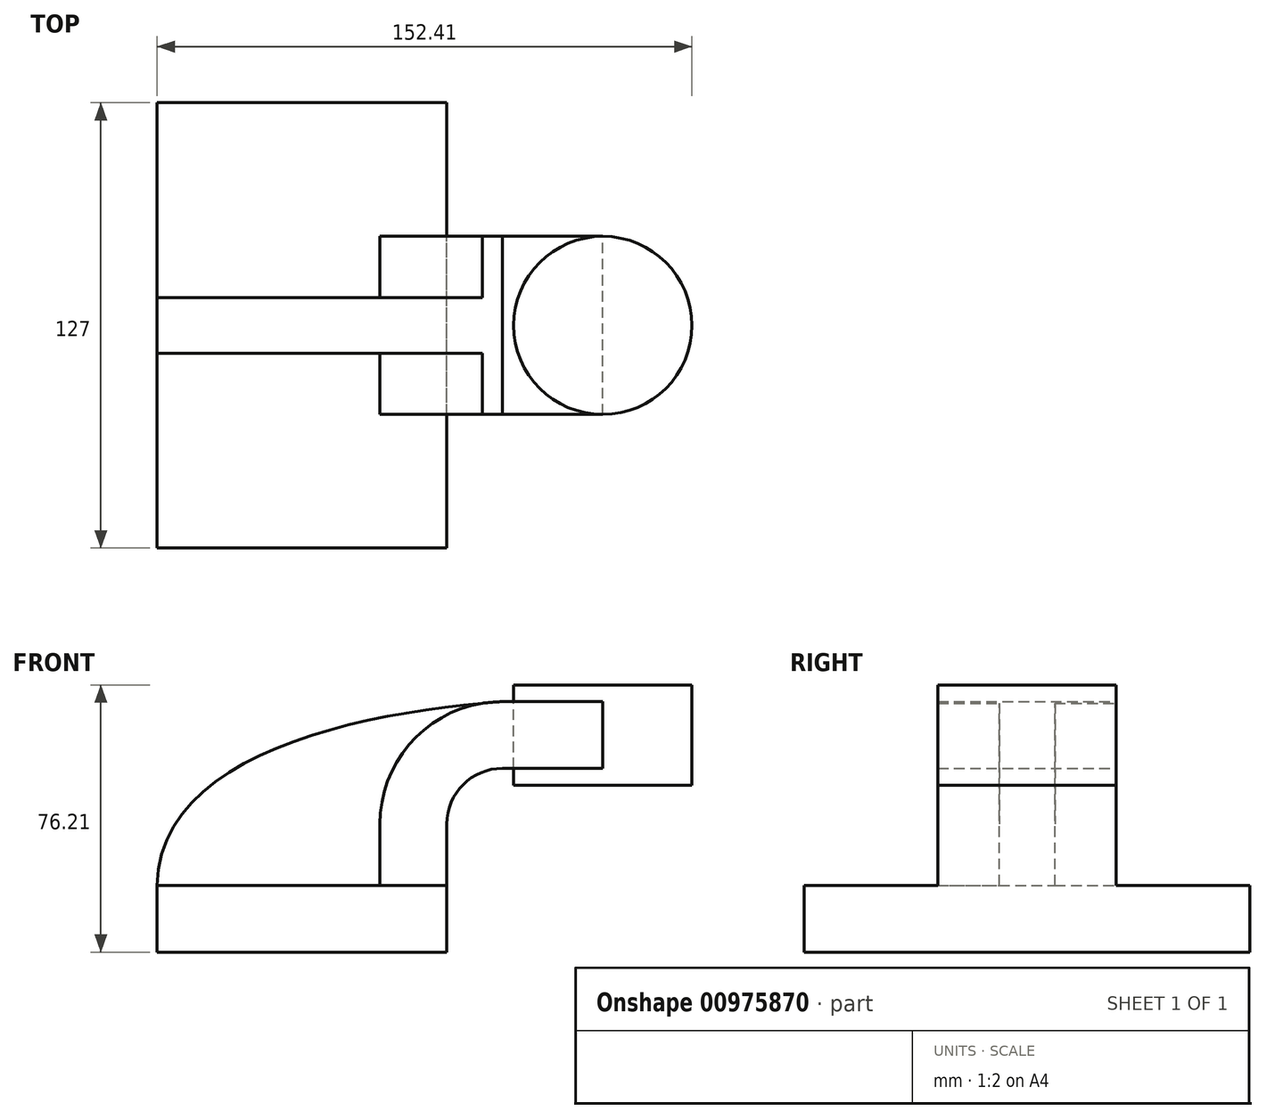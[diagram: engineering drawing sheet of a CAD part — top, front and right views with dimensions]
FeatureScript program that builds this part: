
annotation { "Feature Type Name" : "Feature", "Feature Type Description" : "" }
export const myFeature = defineFeature(function(context is Context, id is Id, definition is map)
    precondition{}
    {
        {
            var Q0;
            Q0=qCreatedBy(makeId("Front.planeOp"),FACE);
            var sketch = newSketch(context, id + "F0", { "sketchPlane" : qUnion([Q0])});
            skLineSegment(sketch, "E0.bottom", {"start": v(41.27, 9.53) * mm, "end": v(-41.28, 9.53) * mm});
            skLineSegment(sketch, "E0.top", {"start": v(41.28, -9.52) * mm, "end": v(-41.27, -9.52) * mm});
            skLineSegment(sketch, "E0.left", {"start": v(41.28, 9.53) * mm, "end": v(41.28, -9.52) * mm});
            skLineSegment(sketch, "E0.right", {"start": v(-41.28, 9.53) * mm, "end": v(-41.27, -9.52) * mm});
            skPoint(sketch, "E0.middle", {"position": v(0, 0) * mm});
            skLineSegment(sketch, "E1.bottom", {"start": v(111.12, 66.68) * mm, "end": v(60.33, 66.68) * mm});
            skLineSegment(sketch, "E1.top", {"start": v(111.12, 38.1) * mm, "end": v(60.33, 38.1) * mm});
            skLineSegment(sketch, "E1.left", {"start": v(111.12, 66.68) * mm, "end": v(111.12, 38.1) * mm});
            skLineSegment(sketch, "E1.right", {"start": v(60.32, 66.68) * mm, "end": v(60.33, 38.1) * mm});
            skPoint(sketch, "E1.middle", {"position": v(85.72, 52.39) * mm});
            skLineSegment(sketch, "E2", {"start": v(41.27, 9.53) * mm, "end": v(41.27, 27) * mm});
            skArc(sketch, "E3", {"start": v(41.27, 27) * mm, "mid": v(45.92, 38.23) * mm, "end": v(57.15, 42.88) * mm});
            skLineSegment(sketch, "E4", {"start": v(57.15, 42.88) * mm, "end": v(85.72, 42.88) * mm});
            skLineSegment(sketch, "E5.0", {"start": v(57.15, 61.93) * mm, "end": v(85.72, 61.93) * mm});
            skArc(sketch, "E5.1", {"start": v(22.22, 27) * mm, "mid": v(32.45, 51.7) * mm, "end": v(57.15, 61.93) * mm});
            skLineSegment(sketch, "E5.2", {"start": v(22.22, 9.53) * mm, "end": v(22.22, 27) * mm});
            skFitSpline(sketch, "E6", {"points": [v(-41.28, 9.53) * mm, v(57.15, 61.93) * mm], "startDerivative": vector(1.83, 113.14) * mm, "endDerivative": vector(121.05, 9) * mm});
            skLineSegment(sketch, "E7", {"start": v(85.72, 61.93) * mm, "end": v(85.72, 42.88) * mm});
            skLineSegment(sketch, "E8", {"start": v(85.72, 61.93) * mm, "end": v(85.72, 66.68) * mm});
            skLineSegment(sketch, "E9", {"start": v(85.72, 42.88) * mm, "end": v(85.73, 38.1) * mm});
            skSolve(sketch);
        }
        {
            var Q0;
            Q0=makeQuery(id+"F0.imprint","IMPRINT",FACE,{"disambiguationData":[TD([[makeQuery(id+"F0.imprint","IMPRINT",EDGE,{"derivedFrom":sQuery(id+"F0.wireOp",EDGE,"E0.top")}),-1.0]])]});
            extrude(context, id + "F1", {"entities" : qUnion([Q0]), "endBound" : BoundingType.SYMMETRIC, "depth" : 127 * mm, "offsetDistance" : 25.4 * mm});
        }
        {
            var Q0;
            {var subQ1=sQuery(id+"F0.wireOp",EDGE,"E2");Q0=makeQuery(id+"F0.imprint","IMPRINT",FACE,{"disambiguationData":[TD([[makeQuery(id+"F0.imprint","IMPRINT",EDGE,{"derivedFrom":subQ1}),1.0]])]});}
            var Q1;
            {var subQ5=sQuery(id+"F0.wireOp",EDGE,"E7");Q1=makeQuery(id+"F0.imprint","IMPRINT",FACE,{"disambiguationData":[TD([[makeQuery(id+"F0.imprint","IMPRINT",EDGE,{"derivedFrom":subQ5}),-1.0]])]});}
            extrude(context, id + "F2", {"entities" : qUnion([Q0, Q1]), "operationType" : NewBodyOperationType.ADD, "endBound" : BoundingType.SYMMETRIC, "depth" : 50.8 * mm, "offsetDistance" : 25.4 * mm});
        }
        {
            var Q0;
            {var subQ3=sQuery(id+"F0.wireOp",EDGE,"E5.2");Q0=makeQuery(id+"F0.imprint","IMPRINT",FACE,{"disambiguationData":[TD([[makeQuery(id+"F0.imprint","IMPRINT",EDGE,{"derivedFrom":subQ3}),1.0]])]});}
            extrude(context, id + "F3", {"entities" : qUnion([Q0]), "operationType" : NewBodyOperationType.ADD, "endBound" : BoundingType.SYMMETRIC, "depth" : 15.88 * mm, "offsetDistance" : 25.4 * mm});
        }
        {
            var Q0;
            {var subQ0=sQuery(id+"F0.wireOp",EDGE,"E1.left");Q0=makeQuery(id+"F0.imprint","IMPRINT",FACE,{"disambiguationData":[TD([[makeQuery(id+"F0.imprint","IMPRINT",EDGE,{"derivedFrom":subQ0}),-1.0]])]});}
            var Q1;
            Q1=sQuery(id+"F0.wireOp",EDGE,"E1.left");
            var Q2;
            Q2=sQuery(id+"F0.wireOp",EDGE,"E7");
            revolve(context, id + "F4", {"surfaceOperationType" : NewSurfaceOperationType.NEW, "entities" : qUnion([Q0]), "surfaceEntities" : qUnion([Q1]), "axis" : qUnion([Q2]), "revolveType" : RevolveType.FULL});
        }
    });
